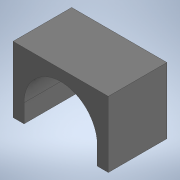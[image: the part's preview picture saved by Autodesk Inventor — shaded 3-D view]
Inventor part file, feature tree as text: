
AUTODESK INVENTOR PART (.ipt)
format: ipt  version: 2021.2 (Build 252289000, 289)  size: 108,544 bytes
history: native  units: in
note: dims shown in document units (in); Inventor stores cm internally (conversion verified against a paired STEP export)
features: extrude x1, sketch x1
ambient origin geometry x8: Origin, YZ Plane, XZ Plane, XY Plane, X Axis, Y Axis, Z Axis, Center Point
bodies: Solid2 (feature_tree)
feature tree (2):
  extrude  "Extrusion3"  Depth=0.075in
  sketch  "Sketch1"  dims[d0=0.25in d2=0.075in d3=0.075in d9=0.4in d10=0.0in]
